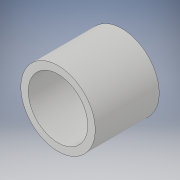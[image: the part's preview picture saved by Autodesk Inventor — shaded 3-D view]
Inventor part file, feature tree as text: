
AUTODESK INVENTOR PART (.ipt)
format: ipt  version: 2019 (Build 230136000, 136)  size: 102,400 bytes
history: native  units: mm
features: extrude x2, sketch x2
ambient origin geometry x8: Origin, YZ Plane, XZ Plane, XY Plane, X Axis, Y Axis, Z Axis, Center Point
bodies: Solid1 (feature_tree)
feature tree (4):
  extrude  "Extrusion1"  Depth=215.0mm TaperAngle=0.0deg
  extrude  "Extrusion2"  Depth=21.5mm TaperAngle=0.0deg
  sketch  "Sketch1"  dims[d0=250.0mm d1=215.0mm d2=0.0mm]
  sketch  "Sketch2"  dims[d3=200.0mm d4=21.5mm d5=0.0mm]
